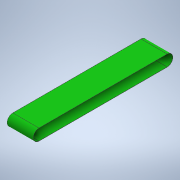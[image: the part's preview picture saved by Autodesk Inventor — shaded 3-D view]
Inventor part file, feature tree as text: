
AUTODESK INVENTOR PART (.ipt)
format: ipt  version: 2020 (Build 240168000, 168)  size: 117,248 bytes
history: native  units: in
note: dims shown in document units (in); Inventor stores cm internally (conversion verified against a paired STEP export)
features: extrude x2, sketch x2
ambient origin geometry x8: Origin, YZ Plane, XZ Plane, XY Plane, X Axis, Y Axis, Z Axis, Center Point
bodies: Solid1 (feature_tree)
feature tree (4):
  extrude  "Extrusion1"  Depth=1.5354in
  extrude  "Extrusion2"  Depth=3.5433in TaperAngle=0.0deg
  sketch  "Sketch1"  dims[d0=1.5354in d1=1.5354in]
  sketch  "Sketch2"  dims[d2=17.3228in d3=3.5433in d4=0.0in d5=1.4961in d6=1.4961in d7=0.0in d8=0.0in]
